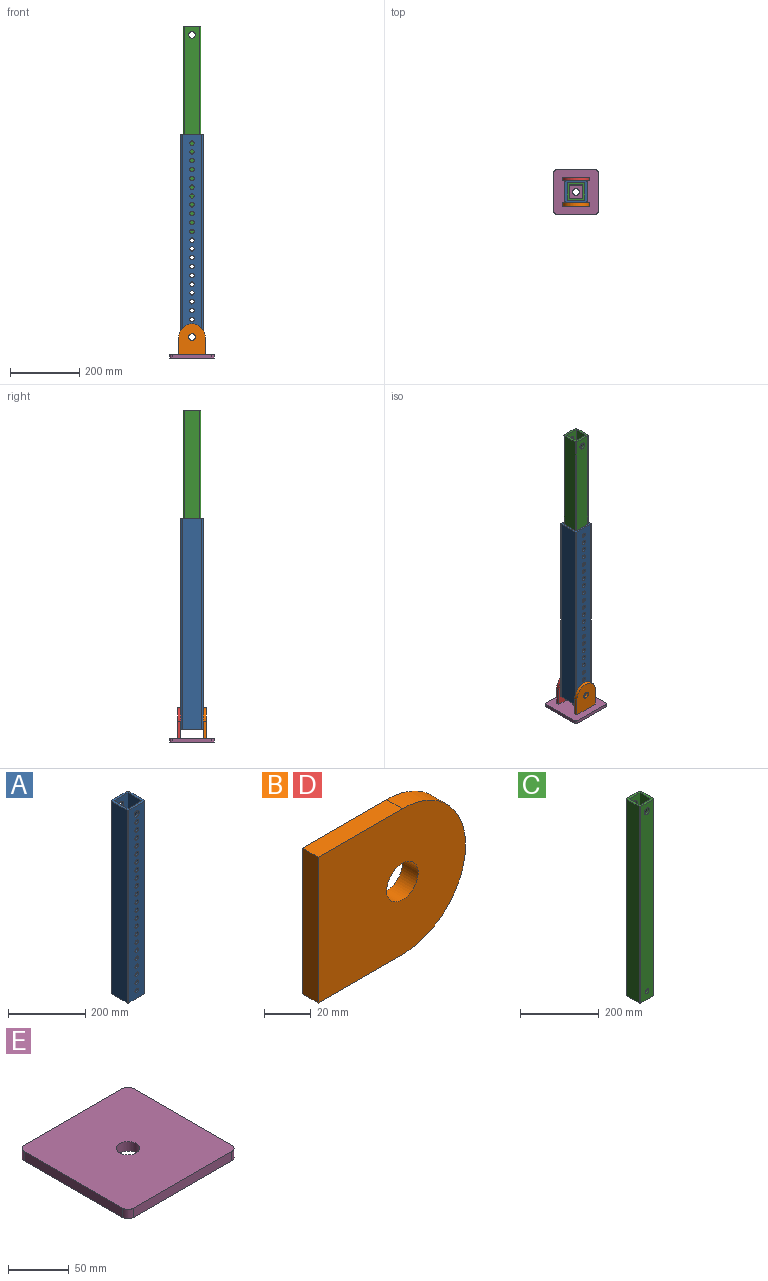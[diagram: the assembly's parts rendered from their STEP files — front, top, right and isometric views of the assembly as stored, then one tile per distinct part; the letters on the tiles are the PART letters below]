
ASSEMBLY  parts=5 mates=6
PART A: 60 faces, bbox 63.5x63.5x609.6 mm
  f0: plane 609.6x57.15mm, normal (1,0,0), area 34838.6mm2, adj f1,f11,f12,f13
  f1: cylinder r=3.17mm len=609.6mm, axis (0,0,-1), area 3040.2mm2, adj f0,f2,f12,f13
  f2: plane 609.6x57.15mm, normal (0,1,0), area 31766.7mm2, adj f1,f3,f12,f13,f14,f15,f16,f17
  f3: cylinder r=3.17mm len=609.6mm, axis (0,0,-1), area 3040.2mm2, adj f2,f4,f12,f13
  f4: plane 609.6x57.15mm, normal (-1,0,0), area 34838.6mm2, adj f3,f5,f12,f13
  f5: cylinder r=3.17mm len=609.6mm, axis (0,0,-1), area 3040.2mm2, adj f4,f6,f12,f13
  f6: plane 609.6x57.15mm, normal (0,-1,0), area 31766.7mm2, adj f5,f11,f12,f13,f36,f37,f38,f39
  f7: plane 609.6x50.8mm, normal (-1,0,0), area 30967.7mm2, adj f8,f10,f12,f13
  f8: plane 609.6x50.8mm, normal (0,1,0), area 27895.8mm2, adj f7,f9,f12,f13,f36,f37,f38,f39
  f9: plane 609.6x50.8mm, normal (1,0,0), area 30967.7mm2, adj f8,f10,f12,f13
  f10: plane 609.6x50.8mm, normal (0,-1,0), area 27895.8mm2, adj f7,f9,f12,f13,f14,f15,f16,f17
  f11: cylinder r=3.17mm len=609.6mm, axis (0,0,-1), area 3040.2mm2, adj f0,f6,f12,f13
  f12: plane 63.5x63.5mm, normal (0,0,1), area 1443mm2, adj f0,f1,f2,f3,f4,f5,f6,f7
  f13: plane 63.5x63.5mm, normal (0,0,-1), area 1443mm2, adj f0,f1,f2,f3,f4,f5,f6,f7
  f14: cylinder r=6.35mm len=12.7mm, axis (0,-1,0), area 253.4mm2, adj f2,f10
  f15: cylinder r=6.35mm len=12.7mm, axis (0,-1,0), area 253.4mm2, adj f2,f10
  f16: cylinder r=6.35mm len=12.7mm, axis (0,-1,0), area 253.4mm2, adj f2,f10
  f17: cylinder r=6.35mm len=12.7mm, axis (0,-1,0), area 253.4mm2, adj f2,f10
  f18: cylinder r=6.35mm len=12.7mm, axis (0,-1,0), area 253.4mm2, adj f2,f10
  f19: cylinder r=6.35mm len=12.7mm, axis (0,-1,0), area 253.4mm2, adj f2,f10
  f20: cylinder r=6.35mm len=12.7mm, axis (0,-1,0), area 253.4mm2, adj f2,f10
  f21: cylinder r=6.35mm len=12.7mm, axis (0,-1,0), area 253.4mm2, adj f2,f10
  f22: cylinder r=6.35mm len=12.7mm, axis (0,-1,0), area 253.4mm2, adj f2,f10
  f23: cylinder r=6.35mm len=12.7mm, axis (0,-1,0), area 253.4mm2, adj f2,f10
  f24: cylinder r=6.35mm len=12.7mm, axis (0,-1,0), area 253.4mm2, adj f2,f10
  f25: cylinder r=6.35mm len=12.7mm, axis (0,-1,0), area 253.4mm2, adj f2,f10
  f26: cylinder r=6.35mm len=12.7mm, axis (0,-1,0), area 253.4mm2, adj f2,f10
  f27: cylinder r=6.35mm len=12.7mm, axis (0,-1,0), area 253.4mm2, adj f2,f10
  f28: cylinder r=6.35mm len=12.7mm, axis (0,-1,0), area 253.4mm2, adj f2,f10
  f29: cylinder r=6.35mm len=12.7mm, axis (0,-1,0), area 253.4mm2, adj f2,f10
  f30: cylinder r=6.35mm len=12.7mm, axis (0,-1,0), area 253.4mm2, adj f2,f10
  f31: cylinder r=6.35mm len=12.7mm, axis (0,-1,0), area 253.4mm2, adj f2,f10
  f32: cylinder r=6.35mm len=12.7mm, axis (0,-1,0), area 253.4mm2, adj f2,f10
  f33: cylinder r=6.35mm len=12.7mm, axis (0,-1,0), area 253.4mm2, adj f2,f10
  f34: cylinder r=6.35mm len=12.7mm, axis (0,-1,0), area 253.4mm2, adj f2,f10
  f35: cylinder r=6.35mm len=12.7mm, axis (0,-1,0), area 253.4mm2, adj f2,f10
  f36: cylinder r=6.35mm len=12.7mm, axis (0,-1,0), area 253.4mm2, adj f6,f8
  f37: cylinder r=6.35mm len=12.7mm, axis (0,-1,0), area 253.4mm2, adj f6,f8
  f38: cylinder r=6.35mm len=12.7mm, axis (0,-1,0), area 253.4mm2, adj f6,f8
  f39: cylinder r=6.35mm len=12.7mm, axis (0,-1,0), area 253.4mm2, adj f6,f8
  f40: cylinder r=6.35mm len=12.7mm, axis (0,-1,0), area 253.4mm2, adj f6,f8
  f41: cylinder r=6.35mm len=12.7mm, axis (0,-1,0), area 253.4mm2, adj f6,f8
  f42: cylinder r=6.35mm len=12.7mm, axis (0,-1,0), area 253.4mm2, adj f6,f8
  f43: cylinder r=6.35mm len=12.7mm, axis (0,-1,0), area 253.4mm2, adj f6,f8
  f44: cylinder r=6.35mm len=12.7mm, axis (0,-1,0), area 253.4mm2, adj f6,f8
  f45: cylinder r=6.35mm len=12.7mm, axis (0,-1,0), area 253.4mm2, adj f6,f8
  f46: cylinder r=6.35mm len=12.7mm, axis (0,-1,0), area 253.4mm2, adj f6,f8
  f47: cylinder r=6.35mm len=12.7mm, axis (0,-1,0), area 253.4mm2, adj f6,f8
  f48: cylinder r=6.35mm len=12.7mm, axis (0,-1,0), area 253.4mm2, adj f6,f8
  f49: cylinder r=6.35mm len=12.7mm, axis (0,-1,0), area 253.4mm2, adj f6,f8
  f50: cylinder r=6.35mm len=12.7mm, axis (0,-1,0), area 253.4mm2, adj f6,f8
  f51: cylinder r=6.35mm len=12.7mm, axis (0,-1,0), area 253.4mm2, adj f6,f8
  f52: cylinder r=6.35mm len=12.7mm, axis (0,-1,0), area 253.4mm2, adj f6,f8
  f53: cylinder r=6.35mm len=12.7mm, axis (0,-1,0), area 253.4mm2, adj f6,f8
  f54: cylinder r=6.35mm len=12.7mm, axis (0,-1,0), area 253.4mm2, adj f6,f8
  f55: cylinder r=6.35mm len=12.7mm, axis (0,-1,0), area 253.4mm2, adj f6,f8
  f56: cylinder r=6.35mm len=12.7mm, axis (0,-1,0), area 253.4mm2, adj f6,f8
  f57: cylinder r=6.35mm len=12.7mm, axis (0,-1,0), area 253.4mm2, adj f6,f8
  f58: cylinder r=9.53mm len=19.05mm, axis (0,1,0), area 380mm2, adj f2,f10
  f59: cylinder r=9.53mm len=19.05mm, axis (0,1,0), area 380mm2, adj f6,f8
PART B: 7 faces, bbox 88.9x9.5x76.2 mm
  f0: plane 76.2x9.53mm, normal (-1,0,0), area 725.8mm2, adj f1,f3,f5,f6
  f1: plane 50.8x9.53mm, normal (0,0,-1), area 483.9mm2, adj f0,f2,f5,f6
  f2: cylinder r=38.1mm len=76.2mm, axis (0,1,0), area 1140.1mm2, adj f1,f3,f5,f6
  f3: plane 50.8x9.53mm, normal (0,0,1), area 483.9mm2, adj f0,f2,f5,f6
  f4: cylinder r=9.53mm len=19.05mm, axis (0,1,0), area 570mm2, adj f5,f6
  f5: plane 88.9x76.2mm, normal (0,-1,0), area 5866.1mm2, adj f0,f1,f2,f3,f4
  f6: plane 88.9x76.2mm, normal (0,1,0), area 5866.1mm2, adj f0,f1,f2,f3,f4
PART C: 18 faces, bbox 50.8x50.8x609.6 mm
  f0: plane 609.6x38.1mm, normal (0,1,0), area 22814.1mm2, adj f1,f11,f12,f13,f16,f17
  f1: plane 609.6x38.1mm, normal (1,0,0), area 23225.8mm2, adj f0,f2,f12,f13
  f2: plane 609.6x38.1mm, normal (0,-1,0), area 22814.1mm2, adj f1,f11,f12,f13,f14,f15
  f3: plane 609.6x44.45mm, normal (-1,0,0), area 27096.7mm2, adj f4,f10,f12,f13
  f4: cylinder r=3.17mm len=609.6mm, axis (0,0,-1), area 3040.2mm2, adj f3,f5,f12,f13
  f5: plane 609.6x44.45mm, normal (0,-1,0), area 26685mm2, adj f4,f6,f12,f13,f16,f17
  f6: cylinder r=3.17mm len=609.6mm, axis (0,0,-1), area 3040.2mm2, adj f5,f7,f12,f13
  f7: plane 609.6x44.45mm, normal (1,0,0), area 27096.7mm2, adj f6,f8,f12,f13
  f8: cylinder r=3.17mm len=609.6mm, axis (0,0,-1), area 3040.2mm2, adj f7,f9,f12,f13
  f9: plane 609.6x44.45mm, normal (0,1,0), area 26685mm2, adj f8,f10,f12,f13,f14,f15
  f10: cylinder r=3.17mm len=609.6mm, axis (0,0,-1), area 3040.2mm2, adj f3,f9,f12,f13
  f11: plane 609.6x38.1mm, normal (-1,0,0), area 23225.8mm2, adj f0,f2,f12,f13
  f12: plane 50.8x50.8mm, normal (0,0,1), area 1120.4mm2, adj f0,f1,f2,f3,f4,f5,f6,f7
  f13: plane 50.8x50.8mm, normal (0,0,-1), area 1120.4mm2, adj f0,f1,f2,f3,f4,f5,f6,f7
  f14: cylinder r=9.53mm len=19.05mm, axis (0,1,0), area 380mm2, adj f2,f9
  f15: cylinder r=6.35mm len=12.7mm, axis (0,1,0), area 253.4mm2, adj f2,f9
  f16: cylinder r=9.53mm len=19.05mm, axis (0,1,0), area 380mm2, adj f0,f5
  f17: cylinder r=6.35mm len=12.7mm, axis (0,1,0), area 253.4mm2, adj f0,f5
PART D: same geometry as B
PART E: 11 faces, bbox 127x127x9.5 mm
  f0: plane 114.3x9.53mm, normal (1,0,0), area 1088.7mm2, adj f1,f8,f9,f10
  f1: cylinder r=6.35mm len=9.53mm, axis (0,0,-1), area 95mm2, adj f0,f2,f9,f10
  f2: plane 114.3x9.53mm, normal (0,1,0), area 1088.7mm2, adj f1,f3,f9,f10
  f3: cylinder r=6.35mm len=9.53mm, axis (0,0,-1), area 95mm2, adj f2,f4,f9,f10
  f4: plane 114.3x9.53mm, normal (-1,0,0), area 1088.7mm2, adj f3,f5,f9,f10
  f5: cylinder r=6.35mm len=9.53mm, axis (0,0,-1), area 95mm2, adj f4,f6,f9,f10
  f6: plane 114.3x9.53mm, normal (0,-1,0), area 1088.7mm2, adj f5,f8,f9,f10
  f7: cylinder r=9.53mm len=19.05mm, axis (0,0,-1), area 570mm2, adj f9,f10
  f8: cylinder r=6.35mm len=9.53mm, axis (0,0,-1), area 95mm2, adj f0,f6,f9,f10
  f9: plane 127x127mm, normal (0,0,1), area 15809.4mm2, adj f0,f1,f2,f3,f4,f5,f6,f7
  f10: plane 127x127mm, normal (0,0,-1), area 15809.4mm2, adj f0,f1,f2,f3,f4,f5,f6,f7
PLACE A rot(axis=(1,0,0),180deg) t=(-487.19,50.65,630.57)mm
PLACE B rot(axis=(0,-1,0),90deg) t=(-422.48,83.2,239.71)mm
PLACE C t=(-663.97,-57.85,332.97)mm
PLACE D rot(axis=(0,-1,0),90deg) t=(-422.48,156.22,239.71)mm
PLACE E t=(-356.33,102.38,-13.96)mm
MATE planar C.f7 <-> A.f7  axis (1,0,0) through (-351.36,114.95,637.77)mm
MATE fastened B.f0 <-> E.f9  axis (0,0,-1) through (-376.76,73.67,-4.43)mm
MATE planar A.f58 <-> D.f2  axis (0,1,0) through (-376.76,146.7,46.37)mm
MATE planar C.f5 <-> A.f14  axis (0,-1,0) through (-376.76,89.55,636.11)mm
MATE cylindrical A.f58 <-> B.f2  axis (0,-1,0) through (-376.76,83.2,46.37)mm
MATE fastened D.f0 <-> E.f9  axis (0,0,-1) through (-376.76,156.22,-4.43)mm
